# Revit family: 3080037
name_source: partatom
category: Lighting Fixtures
revit_build: Autodesk Revit 2016 (Build: 20150220_1215(x64)
units: mm (PartAtom-declared; Revit-internal decimal feet)

## family parameters
Cut with Voids When Loaded = No
Host = Face
Light Source = Yes
OmniClass Number = 23.80.70.11.17
OmniClass Title = Specialized Lighting by Location or Use
Part Type = Normal
Room Calculation Point = No
Round Connector Dimension = Use Diameter
Shared = No

## types (1)
- 3080037 INVERTO DIR/IND NW EB BLACK
    Apparent Load = 30 VA
    Assembly Code = D5020200
    Beam Angle = 40.00°
    Body Material = Aluminum_Sylvania_Inverto_Silver
    CRI ( Ra ) = 80
    Catalog Number = 3080037 Inverto Dir/Ind NW Eb Black
    Color Filter = 16777215
    Default Elevation = 0 mm  [stored 0 ft]
    Description = 16W (low output) or 19W (high output) Direct / indirect luminaire 4 standard colours: Gloss black, Matt white, Satin silver and Matt rust Wire to base with pluggable connection for easy installation Provides a uniform light, while offering a high light output of up to 3233lm (2 x 1616lm) at 107lm/W Comes with a 40° beam as standard. Narrow beam kit available as separate accessory Suitable for looping - See more at: http://www.feilosylvania.com
    Diffuser Material = Polycarbonate_Sylvania_Inverto_Clear
    Dimming Lamp Color Temperature Shift = <None>
    Distribution type = Direct/Indirect
    Drive Current = 350mA
    Electrical Protection = CLASS I
    Energy Class = A++ A+ A
    Height = 220 mm  [stored 0.721785 ft]
    IK Rating = IK02
    IP Rating = IP65
    LOR = 100%
    Lamp Comments = Integrated LED
    Length = 110 mm  [stored 0.360892 ft]
    Life = 50 000h
    Manufacturer = Feilo Sylvania
    Model = Inverto Dir/Ind NW Eb Black
    Photometric Web File = 3080037.ies
    Product Family = Inverto Direct/Indirect
    Product Page URL = http://www.feilosylvania.com
    Ta Rating = -25 to +25
    Tilt Angle = 0.00°
    URL = 0
    Voltage = 240 V
    Voltage Comments = UNV (Universal Voltage; 230-240 Volt)
    Weight = 2.44 kg
    Width = 110 mm  [stored 0.360892 ft]

note: [stored X ft] marks values corroborated as IEEE doubles in the binary element streams (Revit-internal decimal feet)

## geometry (parser evidence)
native form markers: Blend x2, Sweep x2
no freeform markers — native parametric forms only
